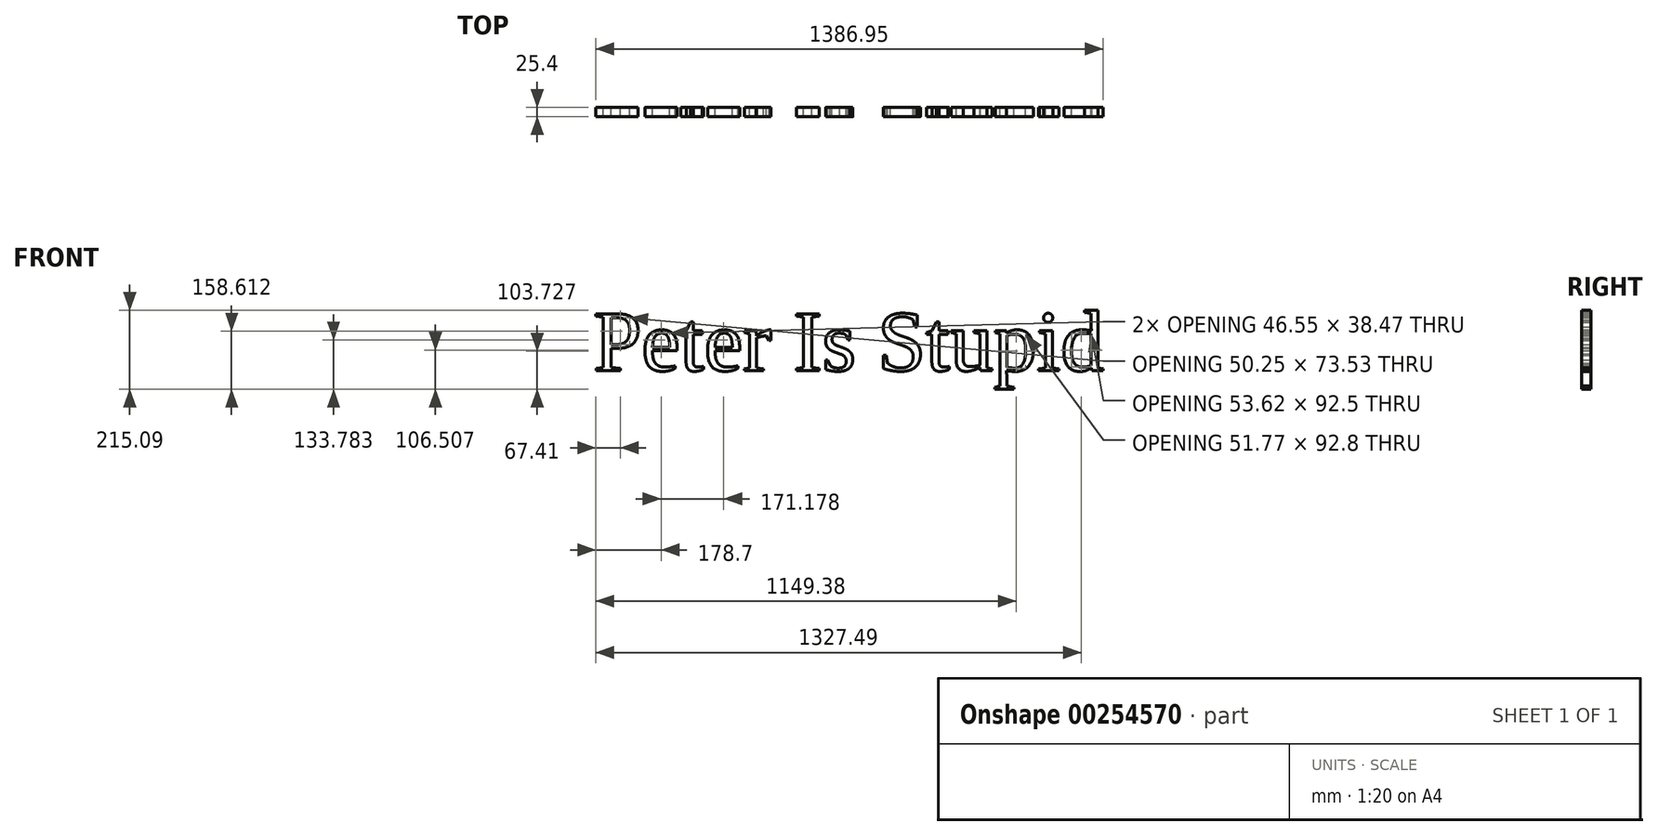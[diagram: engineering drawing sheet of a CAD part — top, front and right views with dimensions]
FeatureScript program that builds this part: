
annotation { "Feature Type Name" : "Feature", "Feature Type Description" : "" }
export const myFeature = defineFeature(function(context is Context, id is Id, definition is map)
    precondition{}
    {
        {
            var Q0;
            Q0=qCreatedBy(makeId("Front.planeOp"),FACE);
            var sketch = newSketch(context, id + "F0", { "sketchPlane" : qUnion([Q0])});
            skText(sketch, "E0", { "text": "Peter Is Stupid", "fontName": "Tinos-Regular.ttf"});
            const initialGuessF0  = {"E0": [-0.15307, -0.0851, 1, 0, 0.17077]};
            skSetInitialGuess(sketch, initialGuessF0);
            skSolve(sketch);
        }
        {
            var Q0;
            Q0 = qSketchRegion(id + "F0", true);
            extrude(context, id + "F1", {"entities" : qUnion([Q0]), "depth" : 25.4 * mm});
        }
    });
